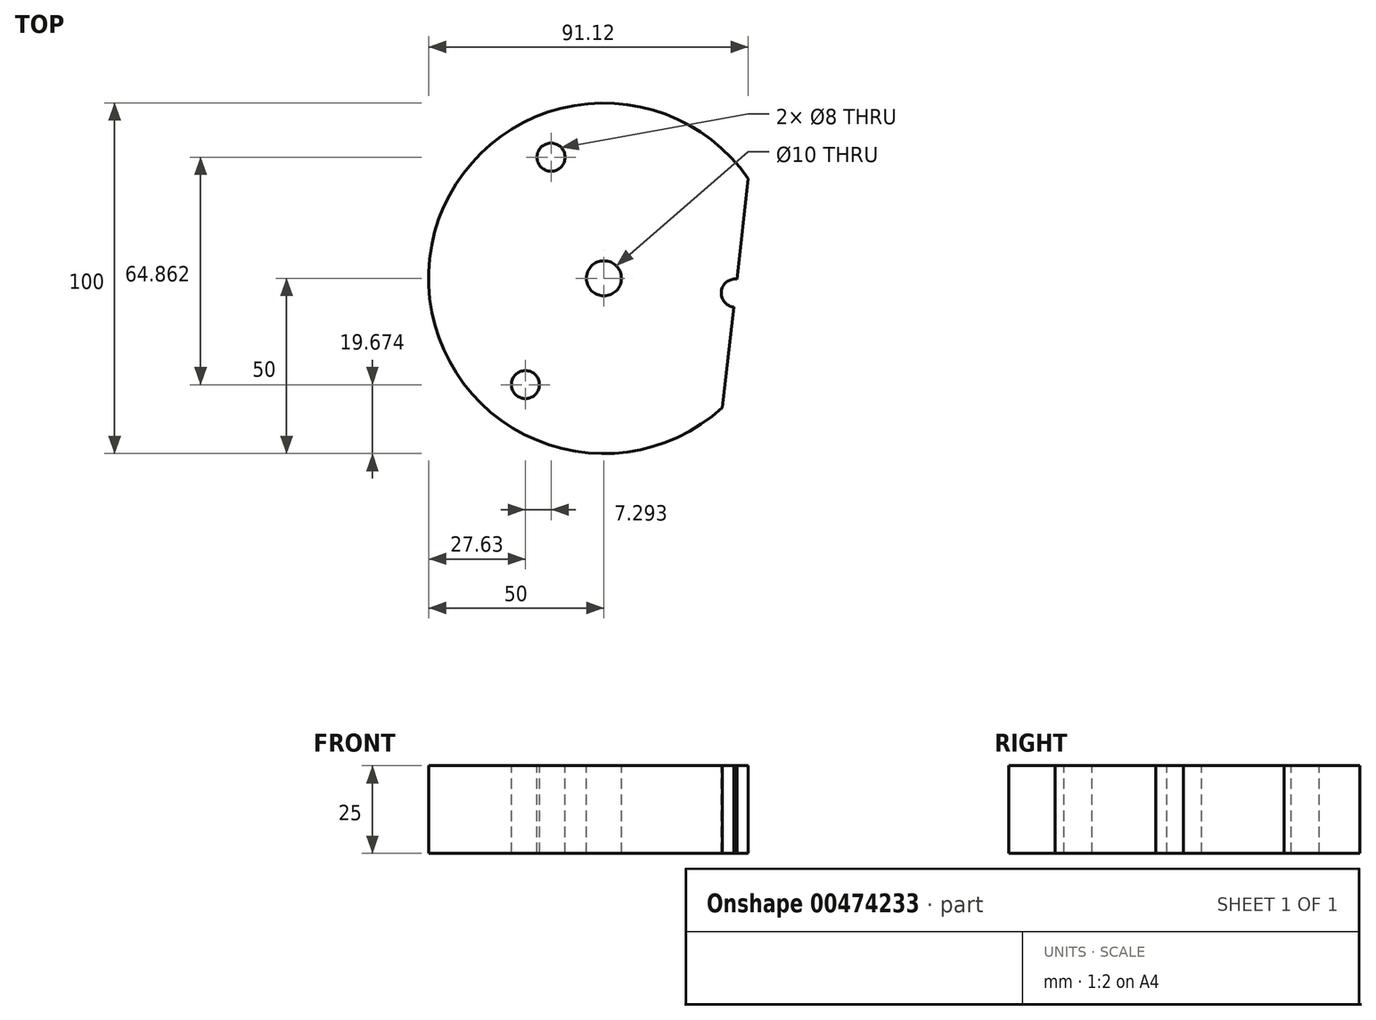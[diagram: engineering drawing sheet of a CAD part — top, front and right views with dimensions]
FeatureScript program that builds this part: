
annotation { "Feature Type Name" : "Feature", "Feature Type Description" : "" }
export const myFeature = defineFeature(function(context is Context, id is Id, definition is map)
    precondition{}
    {
        {
            var Q0;
            Q0=qCreatedBy(makeId("Top.planeOp"),FACE);
            var sketch = newSketch(context, id + "F0", { "sketchPlane" : qUnion([Q0])});
            skCircle(sketch, "E0", {"center": v(0, 0) * mm, "radius": 50 * mm});
            skCircle(sketch, "E1.cCircle", {"center": v(0, 0) * mm, "radius": 37.68 * mm, "construction": true});
            skLineSegment(sketch, "E1.0", {"start": v(-74.9, 8.42) * mm, "end": v(44.74, 60.65) * mm});
            skLineSegment(sketch, "E1.1", {"start": v(44.74, 60.65) * mm, "end": v(30.16, -69.07) * mm});
            skLineSegment(sketch, "E1.2", {"start": v(30.16, -69.07) * mm, "end": v(-74.9, 8.42) * mm});
            skPoint(sketch, "E1.0.midPoint", {"position": v(-15.08, 34.54) * mm});
            skCircle(sketch, "E2", {"center": v(-15.08, 34.54) * mm, "radius": 4 * mm});
            skCircle(sketch, "E3", {"center": v(37.45, -4.21) * mm, "radius": 4 * mm});
            skCircle(sketch, "E4", {"center": v(-22.37, -30.33) * mm, "radius": 4 * mm});
            skSolve(sketch);
        }
        {
            var Q0;
            {var subQ1=sQuery(id+"F0.wireOp",EDGE,"E0");var subQ13=sQuery(id+"F0.wireOp",EDGE,"E1.0");var subQ14=makeQuery(id+"F0.imprint","INTERSECT",VERTEX,{"disambiguationData":[OD(0.0)],"derivedFrom":[subQ1,subQ13]});Q0=makeQuery(id+"F0.imprint","IMPRINT",FACE,{"disambiguationData":[TD([[makeQuery(id+"F0.imprint","IMPRINT",EDGE,{"disambiguationData":[TD([[subQ14,1.0]])],"derivedFrom":subQ1}),1.0]])]});}
            var Q1;
            {var subQ0=sQuery(id+"F0.wireOp",EDGE,"E1.0");var subQ1=sQuery(id+"F0.wireOp",EDGE,"E0");var subQ2=makeQuery(id+"F0.imprint","INTERSECT",VERTEX,{"disambiguationData":[OD(0.0)],"derivedFrom":[subQ1,subQ0]});Q1=makeQuery(id+"F0.imprint","IMPRINT",FACE,{"disambiguationData":[TD([[makeQuery(id+"F0.imprint","IMPRINT",EDGE,{"disambiguationData":[TD([[subQ2,-1.0]])],"derivedFrom":subQ1}),1.0]])]});}
            var Q2;
            {var subQ0=sQuery(id+"F0.wireOp",EDGE,"E1.1");var subQ1=sQuery(id+"F0.wireOp",EDGE,"E0");var subQ2=makeQuery(id+"F0.imprint","INTERSECT",VERTEX,{"disambiguationData":[OD(0.0)],"derivedFrom":[subQ1,subQ0]});Q2=makeQuery(id+"F0.imprint","IMPRINT",FACE,{"disambiguationData":[TD([[makeQuery(id+"F0.imprint","IMPRINT",EDGE,{"disambiguationData":[TD([[subQ2,1.0]])],"derivedFrom":subQ1}),1.0]])]});}
            var Q3;
            {var subQ0=sQuery(id+"F0.wireOp",EDGE,"E1.2");var subQ1=sQuery(id+"F0.wireOp",EDGE,"E0");var subQ2=makeQuery(id+"F0.imprint","INTERSECT",VERTEX,{"disambiguationData":[OD(0.0)],"derivedFrom":[subQ1,subQ0]});Q3=makeQuery(id+"F0.imprint","IMPRINT",FACE,{"disambiguationData":[TD([[makeQuery(id+"F0.imprint","IMPRINT",EDGE,{"disambiguationData":[TD([[subQ2,-1.0]])],"derivedFrom":subQ1}),1.0]])]});}
            extrude(context, id + "F1", {"entities" : qUnion([Q0, Q1, Q2, Q3]), "depth" : -25 * mm});
        }
        {
            var Q0;
            Q0=makeQuery(id+"F1.opExtrude","CAP_FACE",FACE,{"disambiguationData":[OSD([sQuery(id+"F0.wireOp",EDGE,"E0"),sQuery(id+"F0.wireOp",EDGE,"E2"),sQuery(id+"F0.wireOp",EDGE,"E3"),sQuery(id+"F0.wireOp",EDGE,"E4")])],"isStart":true});
            var sketch = newSketch(context, id + "F2", { "sketchPlane" : qUnion([Q0])});
            skCircle(sketch, "E5", {"center": v(0, 0) * mm, "radius": 5 * mm});
            skCircle(sketch, "E6", {"center": v(0, 0) * mm, "radius": 6 * mm});
            skSolve(sketch);
        }
        {
            var Q0;
            Q0=makeQuery(id+"F2.imprint","IMPRINT",FACE,{"disambiguationData":[TD([[makeQuery(id+"F2.imprint","IMPRINT",EDGE,{"derivedFrom":sQuery(id+"F2.wireOp",EDGE,"E5")}),1.0]])]});
            extrude(context, id + "F3", {"entities" : qUnion([Q0]), "operationType" : NewBodyOperationType.REMOVE, "oppositeDirection" : true, "depth" : 40.9 * mm});
        }
    });
